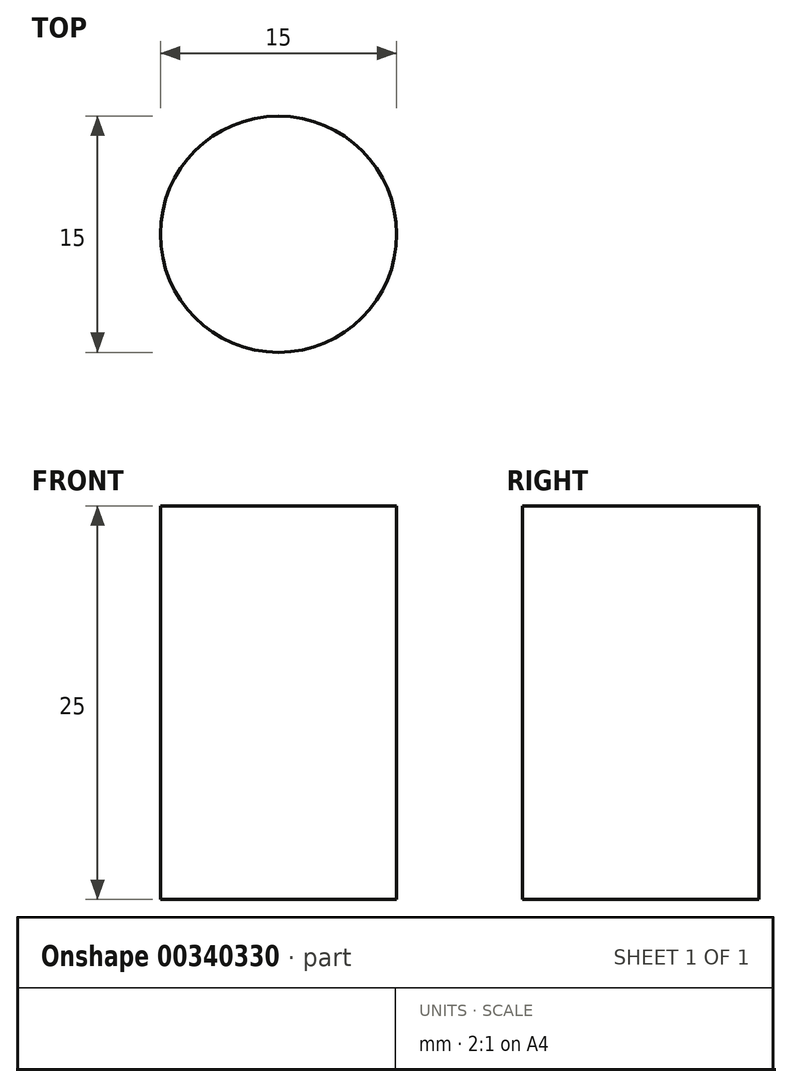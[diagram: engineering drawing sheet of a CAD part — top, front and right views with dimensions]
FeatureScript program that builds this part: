
annotation { "Feature Type Name" : "Feature", "Feature Type Description" : "" }
export const myFeature = defineFeature(function(context is Context, id is Id, definition is map)
    precondition{}
    {
        {
            var Q0;
            Q0=qCreatedBy(makeId("Top.planeOp"),FACE);
            var sketch = newSketch(context, id + "F0", { "sketchPlane" : qUnion([Q0])});
            skCircle(sketch, "E0", {"center": v(0, 0) * mm, "radius": 7.5 * mm});
            skSolve(sketch);
        }
        {
            var Q0;
            Q0=makeQuery(id+"F0.imprint","IMPRINT",FACE,{"disambiguationData":[TD([[makeQuery(id+"F0.imprint","IMPRINT",EDGE,{"derivedFrom":sQuery(id+"F0.wireOp",EDGE,"E0")}),1.0]])]});
            extrude(context, id + "F1", {"entities" : qUnion([Q0]), "depth" : 25 * mm});
        }
    });
